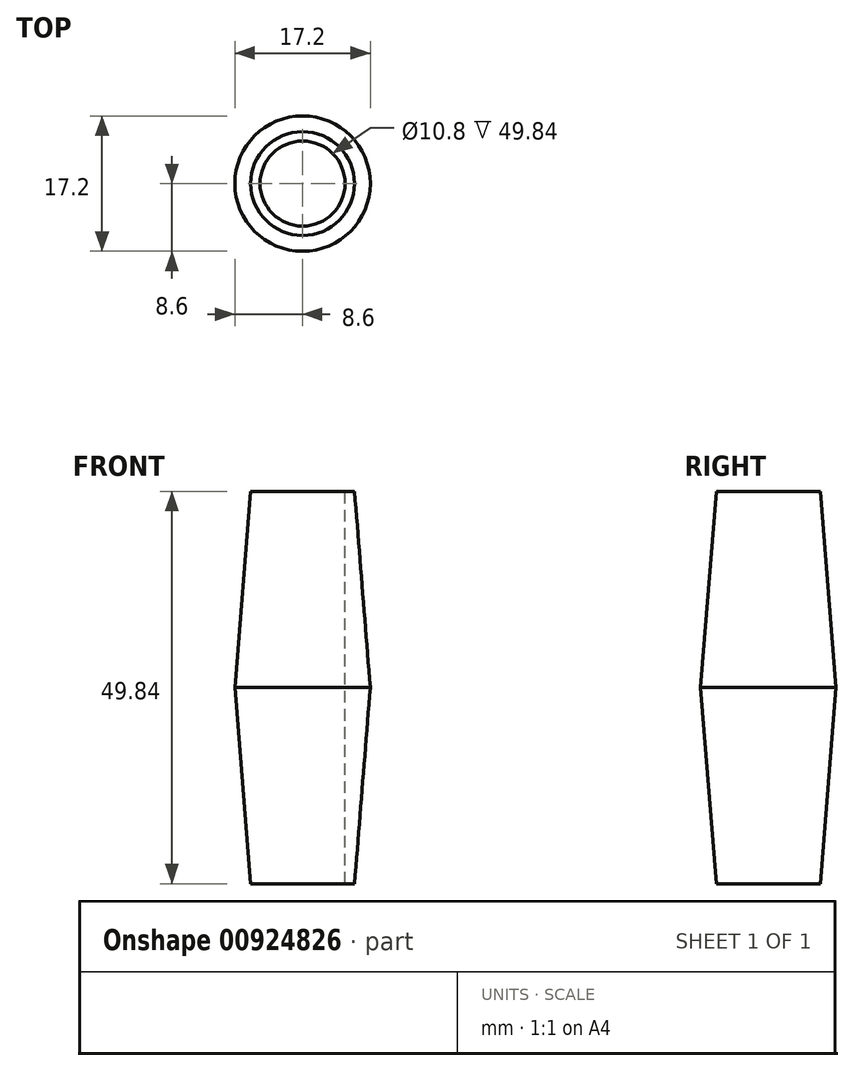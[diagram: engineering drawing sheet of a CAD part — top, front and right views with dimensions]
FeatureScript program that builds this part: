
annotation { "Feature Type Name" : "Feature", "Feature Type Description" : "" }
export const myFeature = defineFeature(function(context is Context, id is Id, definition is map)
    precondition{}
    {
        {
            var Q0;
            Q0=qCreatedBy(makeId("Front.planeOp"),FACE);
            var sketch = newSketch(context, id + "F0", { "sketchPlane" : qUnion([Q0])});
            skLineSegment(sketch, "E0", {"start": v(0, 0) * mm, "end": v(0, 24.92) * mm});
            skLineSegment(sketch, "E1", {"start": v(0, 24.92) * mm, "end": v(-1.2, 24.92) * mm});
            skLineSegment(sketch, "E2", {"start": v(-1.2, 24.92) * mm, "end": v(-3.2, 0) * mm});
            skLineSegment(sketch, "E3", {"start": v(-3.2, 0) * mm, "end": v(-1.2, -24.92) * mm});
            skLineSegment(sketch, "E4", {"start": v(-1.2, -24.92) * mm, "end": v(0, -24.92) * mm});
            skLineSegment(sketch, "E5", {"start": v(0, -24.92) * mm, "end": v(0, 0) * mm});
            skLineSegment(sketch, "E6", {"start": v(0, 0) * mm, "end": v(-3.2, 0) * mm, "construction": true});
            skLineSegment(sketch, "E7", {"start": v(5.4, 35.88) * mm, "end": v(5.4, -45.14) * mm, "construction": true});
            skSolve(sketch);
        }
        {
            var Q0;
            Q0=makeQuery(id+"F0.imprint","IMPRINT",FACE,{"disambiguationData":[TD([[makeQuery(id+"F0.imprint","IMPRINT",EDGE,{"derivedFrom":sQuery(id+"F0.wireOp",EDGE,"E0")}),1.0]])]});
            var Q1;
            Q1=sQuery(id+"F0.wireOp",EDGE,"E7");
            revolve(context, id + "F1", {"surfaceOperationType" : NewSurfaceOperationType.NEW, "entities" : qUnion([Q0]), "axis" : qUnion([Q1]), "revolveType" : RevolveType.FULL});
        }
    });
